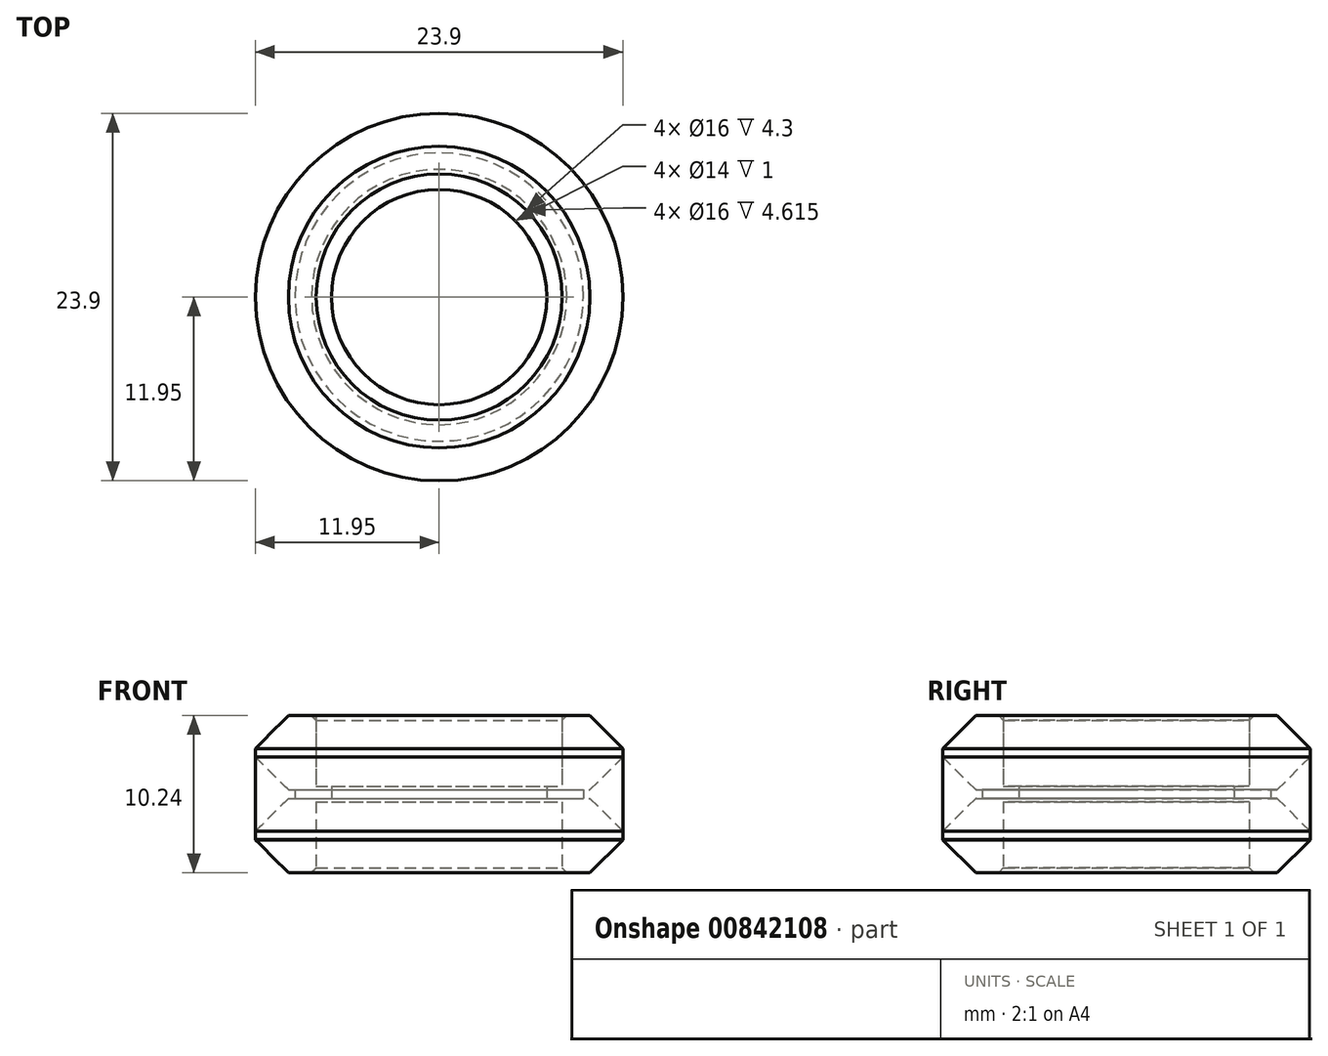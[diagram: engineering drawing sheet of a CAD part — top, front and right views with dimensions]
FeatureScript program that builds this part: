
annotation { "Feature Type Name" : "Feature", "Feature Type Description" : "" }
export const myFeature = defineFeature(function(context is Context, id is Id, definition is map)
    precondition{}
    {
        {
            var Q0;
            Q0=qCreatedBy(makeId("Front.planeOp"),FACE);
            var sketch = newSketch(context, id + "F0", { "sketchPlane" : qUnion([Q0])});
            skLineSegment(sketch, "E0", {"start": v(-8, 5.12) * mm, "end": v(-9.8, 5.12) * mm});
            skLineSegment(sketch, "E1", {"start": v(-9.8, 5.12) * mm, "end": v(-11.95, 2.97) * mm});
            skLineSegment(sketch, "E2", {"start": v(-11.95, 2.97) * mm, "end": v(-11.95, 2.42) * mm});
            skLineSegment(sketch, "E3", {"start": v(-11.95, -2.97) * mm, "end": v(-9.8, -5.11) * mm});
            skLineSegment(sketch, "E4", {"start": v(-9.8, -5.12) * mm, "end": v(-8, -5.12) * mm});
            skLineSegment(sketch, "E5", {"start": v(0, -5.12) * mm, "end": v(0, 5.12) * mm, "construction": true});
            skLineSegment(sketch, "E6", {"start": v(0, 0) * mm, "end": v(-9.47, 0) * mm, "construction": true});
            skLineSegment(sketch, "E7", {"start": v(-8, 5.12) * mm, "end": v(-8, 0.5) * mm});
            skLineSegment(sketch, "E8", {"start": v(-8, 0.5) * mm, "end": v(-7, 0.5) * mm});
            skLineSegment(sketch, "E9", {"start": v(-7, 0.5) * mm, "end": v(-7, -0.5) * mm});
            skLineSegment(sketch, "E10", {"start": v(-7, -0.5) * mm, "end": v(-8, -0.5) * mm});
            skLineSegment(sketch, "E11", {"start": v(-8, -0.5) * mm, "end": v(-8, -5.12) * mm});
            skLineSegment(sketch, "E12", {"start": v(-11.95, -2.42) * mm, "end": v(-11.95, -2.97) * mm});
            skLineSegment(sketch, "E13", {"start": v(-9.8, -0.27) * mm, "end": v(-11.95, -2.42) * mm});
            skLineSegment(sketch, "E14", {"start": v(-11.95, 2.42) * mm, "end": v(-9.8, 0.28) * mm});
            skLineSegment(sketch, "E15", {"start": v(-9.8, -0.27) * mm, "end": v(-9.38, -0.27) * mm});
            skLineSegment(sketch, "E16", {"start": v(-9.38, -0.27) * mm, "end": v(-9.38, 0.28) * mm});
            skLineSegment(sketch, "E17", {"start": v(-9.38, 0.28) * mm, "end": v(-9.8, 0.28) * mm});
            skSolve(sketch);
        }
        {
            var Q0;
            Q0=qCreatedBy(makeId("Front.planeOp"),FACE);
            var sketch = newSketch(context, id + "F1", { "sketchPlane" : qUnion([Q0])});
            skLineSegment(sketch, "E18", {"start": v(-8.3, 5.1) * mm, "end": v(-9.8, 5.1) * mm});
            skLineSegment(sketch, "E19", {"start": v(-9.8, 5.1) * mm, "end": v(-11.95, 2.95) * mm});
            skLineSegment(sketch, "E20", {"start": v(-11.95, 2.95) * mm, "end": v(-11.95, -2.95) * mm});
            skLineSegment(sketch, "E21", {"start": v(-11.95, -2.95) * mm, "end": v(-9.8, -5.1) * mm});
            skLineSegment(sketch, "E22", {"start": v(-9.8, -5.1) * mm, "end": v(-8.3, -5.1) * mm});
            skLineSegment(sketch, "E23", {"start": v(0, -5.1) * mm, "end": v(0, 5.1) * mm, "construction": true});
            skLineSegment(sketch, "E24", {"start": v(0, 0) * mm, "end": v(-5.4, 0) * mm, "construction": true});
            skLineSegment(sketch, "E25", {"start": v(-8, 4.8) * mm, "end": v(-8, 0.5) * mm});
            skLineSegment(sketch, "E26", {"start": v(-8, 0.5) * mm, "end": v(-7, 0.5) * mm});
            skLineSegment(sketch, "E27", {"start": v(-7, 0.5) * mm, "end": v(-7, -0.5) * mm});
            skLineSegment(sketch, "E28", {"start": v(-7, -0.5) * mm, "end": v(-8, -0.5) * mm});
            skLineSegment(sketch, "E29", {"start": v(-8, -0.5) * mm, "end": v(-8, -5.1) * mm});
            skLineSegment(sketch, "E30", {"start": v(-8.3, 5.1) * mm, "end": v(-8, 4.8) * mm});
            skLineSegment(sketch, "E31.MirrorCS", {"start": v(-8.3, -5.1) * mm, "end": v(-8, -4.8) * mm});
            skSolve(sketch);
        }
        {
            var Q0;
            Q0=qSketchRegion(id+"F1",true);
            var Q1;
            Q1=sQuery(id+"F1.wireOp",EDGE,"E23");
            revolve(context, id + "F2", {"entities" : qUnion([Q0]), "axis" : qUnion([Q1]), "revolveType" : RevolveType.FULL});
        }
        {
            var Q0;
            Q0=makeQuery(id+"F0.imprint","IMPRINT",FACE,{"disambiguationData":[TD([[makeQuery(id+"F0.imprint","IMPRINT",EDGE,{"derivedFrom":sQuery(id+"F0.wireOp",EDGE,"E0")}),1.0]])]});
            var Q1;
            Q1=sQuery(id+"F0.wireOp",EDGE,"E5");
            revolve(context, id + "F3", {"entities" : qUnion([Q0]), "axis" : qUnion([Q1]), "revolveType" : RevolveType.FULL});
        }
        {
            var Q0;
            Q0=makeQuery(id+"F0.imprint","IMPRINT",FACE,{"disambiguationData":[TD([[makeQuery(id+"F0.imprint","IMPRINT",EDGE,{"derivedFrom":sQuery(id+"F0.wireOp",EDGE,"E0")}),1.0]])]});
            var Q1;
            Q1=sQuery(id+"F0.wireOp",EDGE,"E5");
            revolve(context, id + "F4", {"entities" : qUnion([Q0]), "axis" : qUnion([Q1]), "revolveType" : RevolveType.FULL});
        }
        {
            var Q0;
            Q0=makeQuery(id+"F1.imprint","IMPRINT",FACE,{"disambiguationData":[TD([[makeQuery(id+"F1.imprint","IMPRINT",EDGE,{"derivedFrom":sQuery(id+"F1.wireOp",EDGE,"E18")}),1.0]])]});
            var Q1;
            Q1=sQuery(id+"F1.wireOp",EDGE,"E23");
            revolve(context, id + "F5", {"entities" : qUnion([Q0]), "axis" : qUnion([Q1]), "revolveType" : RevolveType.FULL});
        }
    });
